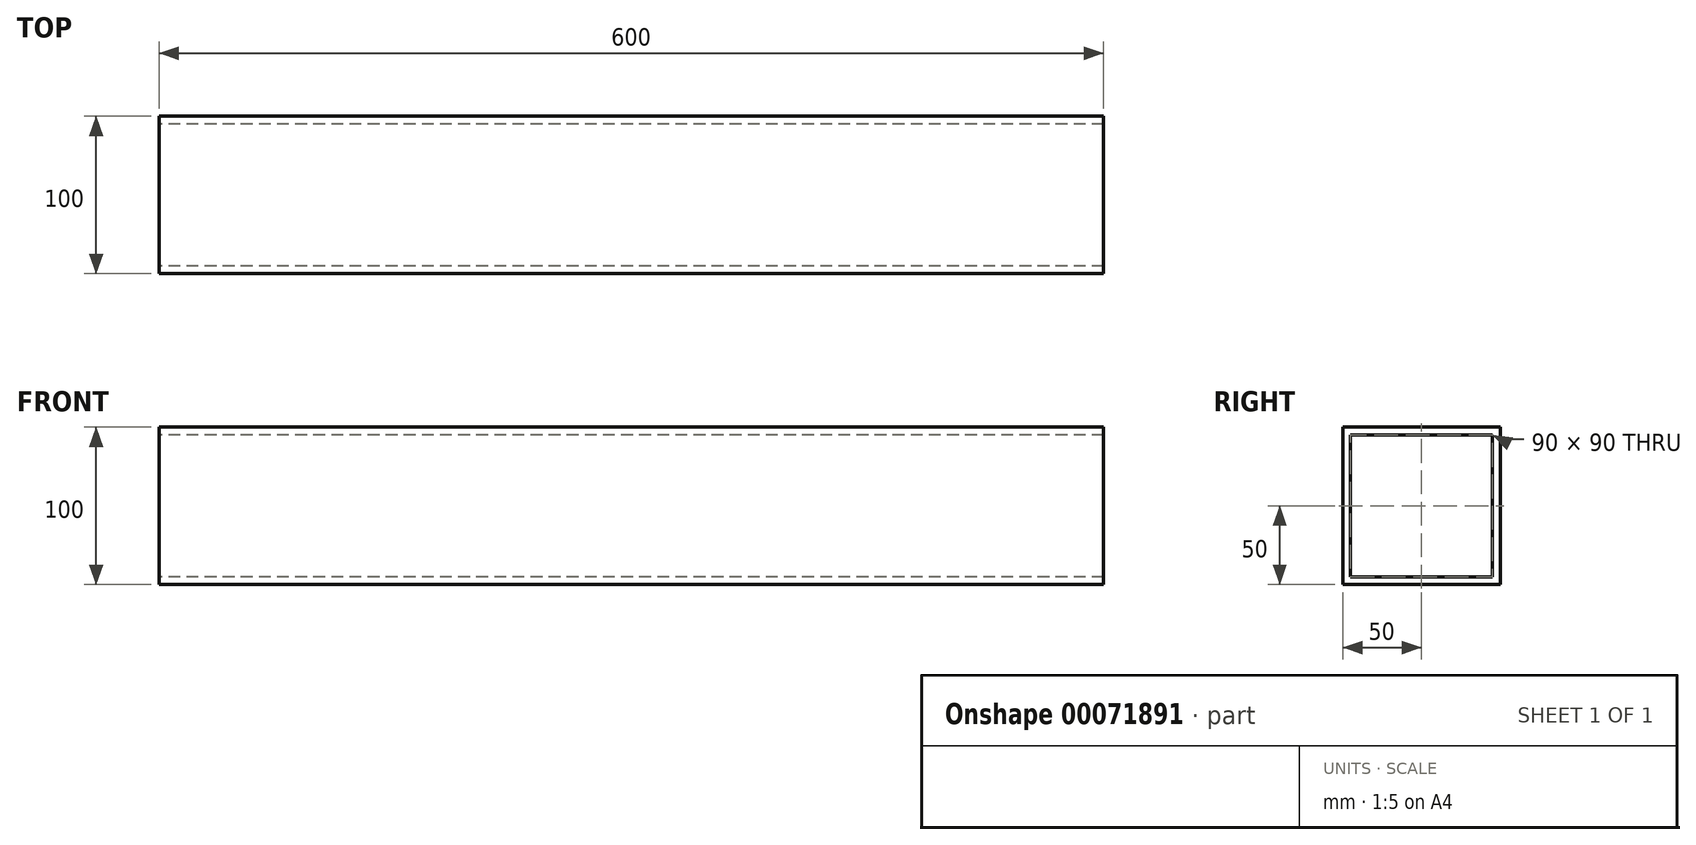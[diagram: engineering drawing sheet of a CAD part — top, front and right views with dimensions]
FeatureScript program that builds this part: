
annotation { "Feature Type Name" : "Feature", "Feature Type Description" : "" }
export const myFeature = defineFeature(function(context is Context, id is Id, definition is map)
    precondition{}
    {
        {
            var Q0;
            Q0=qCreatedBy(makeId("Right.planeOp"),FACE);
            var sketch = newSketch(context, id + "F0", { "sketchPlane" : qUnion([Q0])});
            skLineSegment(sketch, "E0.bottom", {"start": v(50, -50) * mm, "end": v(-50, -50) * mm});
            skLineSegment(sketch, "E0.top", {"start": v(50, 50) * mm, "end": v(-50, 50) * mm});
            skLineSegment(sketch, "E0.left", {"start": v(50, -50) * mm, "end": v(50, 50) * mm});
            skLineSegment(sketch, "E0.right", {"start": v(-50, -50) * mm, "end": v(-50, 50) * mm});
            skPoint(sketch, "E0.middle", {"position": v(0, 0) * mm});
            skLineSegment(sketch, "E1.bottom", {"start": v(-45, 45) * mm, "end": v(45, 45) * mm});
            skLineSegment(sketch, "E1.top", {"start": v(-45, -45) * mm, "end": v(45, -45) * mm});
            skLineSegment(sketch, "E1.left", {"start": v(-45, 45) * mm, "end": v(-45, -45) * mm});
            skLineSegment(sketch, "E1.right", {"start": v(45, 45) * mm, "end": v(45, -45) * mm});
            skSolve(sketch);
        }
        {
            var Q0;
            Q0=qSketchRegion(id+"F0",true);
            extrude(context, id + "F1", {"entities" : qUnion([Q0]), "depth" : 600 * mm});
        }
    });
